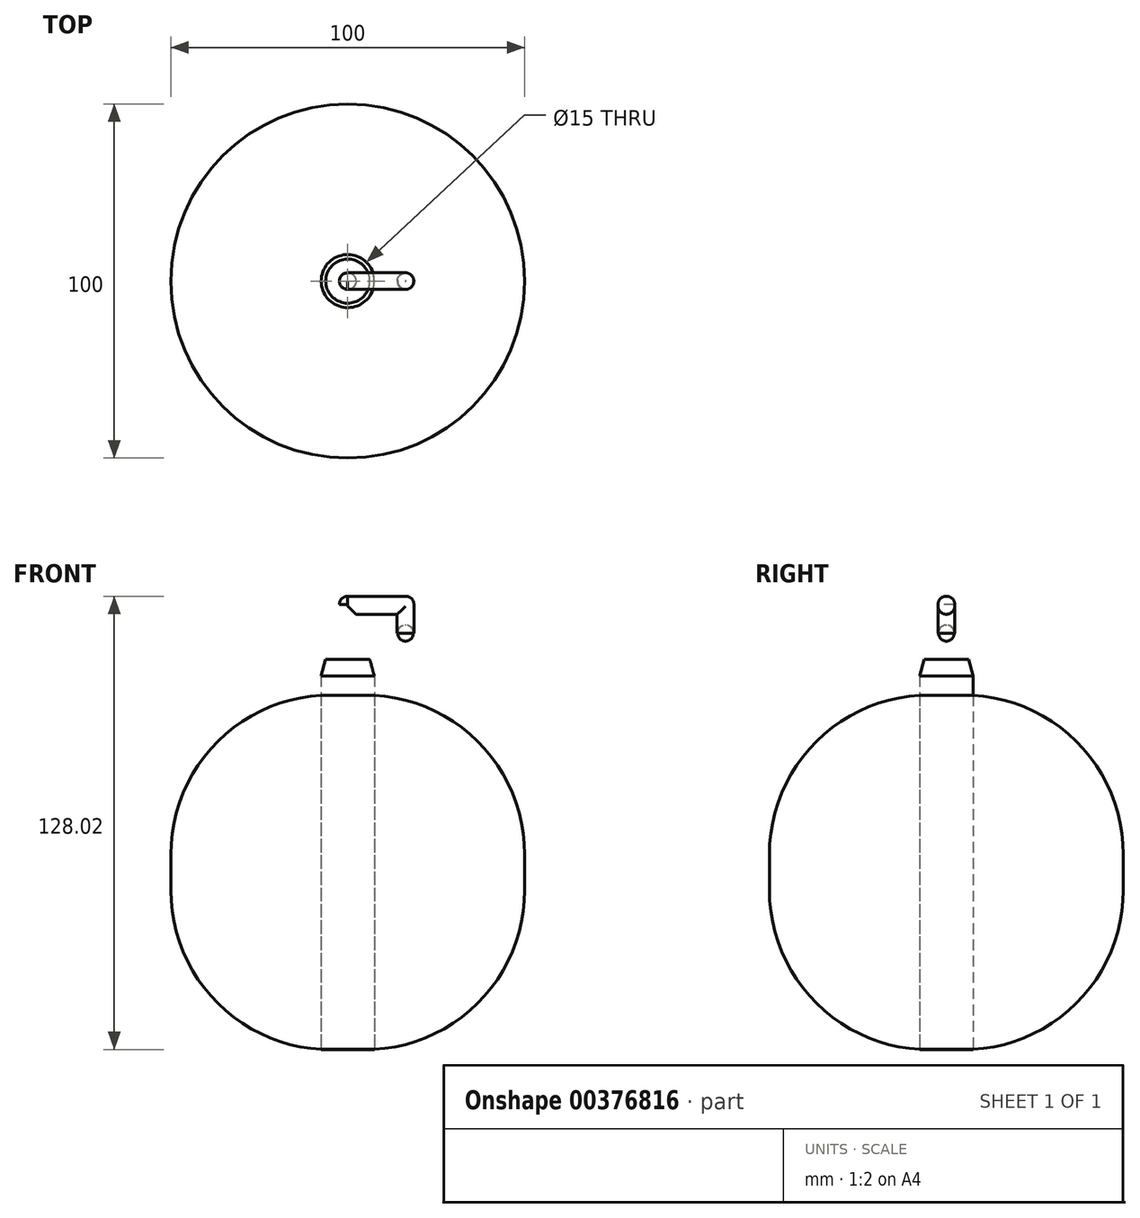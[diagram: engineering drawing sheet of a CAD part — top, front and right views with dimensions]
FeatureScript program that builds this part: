
annotation { "Feature Type Name" : "Feature", "Feature Type Description" : "" }
export const myFeature = defineFeature(function(context is Context, id is Id, definition is map)
    precondition{}
    {
        {
            var Q0;
            Q0=qCreatedBy(makeId("Top.planeOp"),FACE);
            var sketch = newSketch(context, id + "F0", { "sketchPlane" : qUnion([Q0])});
            skCircle(sketch, "E0", {"center": v(0, 0) * mm, "radius": 50 * mm});
            skCircle(sketch, "E1", {"center": v(0, 0) * mm, "radius": 7.5 * mm});
            skCircle(sketch, "E2", {"center": v(0, 0) * mm, "radius": 2.35 * mm});
            skSolve(sketch);
        }
        {
            var Q0;
            Q0=makeQuery(id+"F0.imprint","IMPRINT",FACE,{"disambiguationData":[TD([[makeQuery(id+"F0.imprint","IMPRINT",EDGE,{"derivedFrom":sQuery(id+"F0.wireOp",EDGE,"E0")}),1.0]])]});
            extrude(context, id + "F1", {"entities" : qUnion([Q0]), "endBound" : BoundingType.SYMMETRIC, "depth" : 100 * mm});
        }
        {
            var Q0;
            Q0=makeQuery(id+"F1.opExtrude","CAP_EDGE",EDGE,{"disambiguationData":[OSD([sQuery(id+"F0.wireOp",EDGE,"E0")])],"isStart":false});
            var Q1;
            Q1=makeQuery(id+"F1.opExtrude","SWEPT_FACE",FACE,{"disambiguationData":[OSD([sQuery(id+"F0.wireOp",EDGE,"E0")])]});
            fillet(context, id + "F2", {"entities" : qUnion([Q0, Q1]), "radius" : 45 * mm, "tangentPropagation" : true, "allowEdgeOverflow" : false});
        }
        {
            var Q0;
            Q0=makeQuery(id+"F0.imprint","IMPRINT",FACE,{"disambiguationData":[TD([[makeQuery(id+"F0.imprint","IMPRINT",EDGE,{"derivedFrom":sQuery(id+"F0.wireOp",EDGE,"E1")}),1.0]])]});
            extrude(context, id + "F3", {"entities" : qUnion([Q0]), "endBound" : BoundingType.SYMMETRIC, "depth" : 100.08 * mm});
        }
        {
            var Q0;
            Q0=makeQuery(id+"F0.imprint","IMPRINT",FACE,{"disambiguationData":[TD([[makeQuery(id+"F0.imprint","IMPRINT",EDGE,{"derivedFrom":sQuery(id+"F0.wireOp",EDGE,"E2")}),1.0]])]});
            extrude(context, id + "F4", {"entities" : qUnion([Q0]), "endBound" : BoundingType.SYMMETRIC, "depth" : 100.08 * mm});
        }
        {
            var Q0;
            Q0=makeQuery(id+"F3.opExtrude","CAP_FACE",FACE,{"disambiguationData":[OSD([sQuery(id+"F0.wireOp",EDGE,"E1"),sQuery(id+"F0.wireOp",EDGE,"E2")])],"isStart":false});
            extrude(context, id + "F5", {"entities" : qUnion([Q0]), "operationType" : NewBodyOperationType.ADD, "depth" : 10.16 * mm});
        }
        {
            var Q0;
            Q0=makeQuery(id+"F4.opExtrude","CAP_FACE",FACE,{"disambiguationData":[OSD([sQuery(id+"F0.wireOp",EDGE,"E2")])],"isStart":false});
            extrude(context, id + "F6", {"entities" : qUnion([Q0]), "operationType" : NewBodyOperationType.ADD, "depth" : 25.4 * mm});
        }
        {
            var Q0;
            Q0=makeQuery(id+"F6.opExtrude","CAP_FACE",FACE,{"disambiguationData":[OSD([sQuery(id+"F0.wireOp",EDGE,"E2")])],"isStart":false});
            var sketch = newSketch(context, id + "F7", { "sketchPlane" : qUnion([Q0])});
            skCircle(sketch, "E3", {"center": v(16.33, 0) * mm, "radius": 2.36 * mm});
            skLineSegment(sketch, "E4", {"start": v(0, 2.35) * mm, "end": v(16.33, 2.36) * mm});
            skLineSegment(sketch, "E5", {"start": v(0, -2.35) * mm, "end": v(16.33, -2.36) * mm});
            skLineSegment(sketch, "E6", {"start": v(16.33, -2.36) * mm, "end": v(16.33, 2.36) * mm});
            skLineSegment(sketch, "E7", {"start": v(0, 2.35) * mm, "end": v(0, -2.35) * mm});
            skSolve(sketch);
        }
        {
            var Q0;
            {var subQ1=sQuery(id+"F7.wireOp",EDGE,"E4");Q0=makeQuery(id+"F7.imprint","IMPRINT",FACE,{"disambiguationData":[TD([[makeQuery(id+"F7.imprint","IMPRINT",EDGE,{"derivedFrom":subQ1}),-1.0]])]});}
            var Q1;
            {var subQ0=sQuery(id+"F7.wireOp",EDGE,"E7");Q1=makeQuery(id+"F7.imprint","IMPRINT",FACE,{"disambiguationData":[TD([[makeQuery(id+"F7.imprint","IMPRINT",EDGE,{"derivedFrom":subQ0}),-1.0]])]});}
            var Q2;
            {var subQ0=sQuery(id+"F7.wireOp",EDGE,"E7");Q2=makeQuery(id+"F7.imprint","IMPRINT",FACE,{"disambiguationData":[TD([[makeQuery(id+"F7.imprint","IMPRINT",EDGE,{"derivedFrom":subQ0}),1.0]])]});}
            var Q3;
            {var subQ0=sQuery(id+"F7.wireOp",EDGE,"E6");Q3=makeQuery(id+"F7.imprint","IMPRINT",FACE,{"disambiguationData":[TD([[makeQuery(id+"F7.imprint","IMPRINT",EDGE,{"derivedFrom":subQ0}),-1.0]])]});}
            var Q4;
            {var subQ0=sQuery(id+"F7.wireOp",EDGE,"E6");Q4=makeQuery(id+"F7.imprint","IMPRINT",FACE,{"disambiguationData":[TD([[makeQuery(id+"F7.imprint","IMPRINT",EDGE,{"derivedFrom":subQ0}),1.0]])]});}
            extrude(context, id + "F8", {"entities" : qUnion([Q0, Q1, Q2, Q3, Q4]), "operationType" : NewBodyOperationType.ADD, "depth" : 2.54 * mm});
        }
        {
            var Q0;
            {var subQ0=sQuery(id+"F7.wireOp",EDGE,"E6");Q0=makeQuery(id+"F7.imprint","IMPRINT",FACE,{"disambiguationData":[TD([[makeQuery(id+"F7.imprint","IMPRINT",EDGE,{"derivedFrom":subQ0}),1.0]])]});}
            var Q1;
            {var subQ0=sQuery(id+"F7.wireOp",EDGE,"E6");Q1=makeQuery(id+"F7.imprint","IMPRINT",FACE,{"disambiguationData":[TD([[makeQuery(id+"F7.imprint","IMPRINT",EDGE,{"derivedFrom":subQ0}),-1.0]])]});}
            extrude(context, id + "F9", {"entities" : qUnion([Q0, Q1]), "operationType" : NewBodyOperationType.ADD, "oppositeDirection" : true, "depth" : 10.16 * mm});
        }
        {
            var Q0;
            Q0=makeQuery(id+"F5.opExtrude","CAP_EDGE",EDGE,{"disambiguationData":[OSD([sQuery(id+"F0.wireOp",EDGE,"E1")])],"isStart":false});
            chamfer(context, id + "F10", {"entities" : qUnion([Q0]), "chamferType" : ChamferType.OFFSET_ANGLE, "width" : 1.27 * mm, "oppositeDirection" : false, "angle" : 75 * degree, "tangentPropagation" : true});
        }
        {
            var Q0;
            Q0=makeQuery(id+"F8.opExtrude","CAP_FACE",FACE,{"disambiguationData":[OSD([sQuery(id+"F0.wireOp",EDGE,"E2"),sQuery(id+"F7.wireOp",EDGE,"E3"),sQuery(id+"F7.wireOp",EDGE,"E4"),sQuery(id+"F7.wireOp",EDGE,"E5")])],"isStart":false});
            fillet(context, id + "F11", {"entities" : qUnion([Q0]), "radius" : 2.3 * mm, "tangentPropagation" : true, "allowEdgeOverflow" : false});
        }
        {
            var Q0;
            Q0=makeQuery(id+"F9.opExtrude","CAP_EDGE",EDGE,{"disambiguationData":[OSD([sQuery(id+"F7.wireOp",EDGE,"E3")])],"isStart":false});
            fillet(context, id + "F12", {"entities" : qUnion([Q0]), "radius" : 2.3 * mm, "tangentPropagation" : true, "allowEdgeOverflow" : false});
        }
        {
            var Q0;
            {var subQ1=sQuery(id+"F7.wireOp",EDGE,"E4");Q0=makeQuery(id+"F7.imprint","IMPRINT",FACE,{"disambiguationData":[TD([[makeQuery(id+"F7.imprint","IMPRINT",EDGE,{"derivedFrom":subQ1}),-1.0]])]});}
            extrude(context, id + "F13", {"entities" : qUnion([Q0]), "operationType" : NewBodyOperationType.ADD, "oppositeDirection" : true, "depth" : 2.54 * mm});
        }
        {
            var Q0;
            Q0=makeQuery(id+"F13.opExtrude","CAP_EDGE",EDGE,{"disambiguationData":[OSD([sQuery(id+"F7.wireOp",EDGE,"E4")])],"isStart":false});
            var Q1;
            Q1=makeQuery(id+"F13.opExtrude","CAP_EDGE",EDGE,{"disambiguationData":[OSD([sQuery(id+"F7.wireOp",EDGE,"E5")])],"isStart":false});
            fillet(context, id + "F14", {"entities" : qUnion([Q0, Q1]), "radius" : 2.3 * mm, "allowEdgeOverflow" : false});
        }
    });
